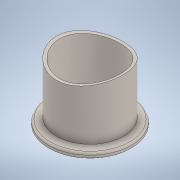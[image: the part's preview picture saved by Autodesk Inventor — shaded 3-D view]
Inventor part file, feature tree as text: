
AUTODESK INVENTOR PART (.ipt)
format: ipt  version: 2021 (Build 250183000, 183)  size: 174,080 bytes
history: native  units: in
note: dims shown in document units (in); Inventor stores cm internally (conversion verified against a paired STEP export)
features: extrude x2, sketch x2, chamfer x1
ambient origin geometry x8: Origin, YZ Plane, XZ Plane, XY Plane, X Axis, Y Axis, Z Axis, Center Point
bodies: Solid1 (feature_tree)
feature tree (5):
  extrude  "Extrusion1"  Depth=0.3937in
  extrude  "Extrusion2"  [1 undecoded]
  sketch  "Sketch1"  dims[d0=0.3937in d1=0.0in d2=6.063in]
  sketch  "Sketch2"  dims[d3=0.0in d4=0.0in]
  chamfer  "Chamfer2"  [1 undecoded]
note: 2 required parameter values undecoded (feature->parameter linkage not recoverable at this tier; creation-order binding heuristic only, values carry confidence <= 0.55)
